# Revit family: V81A-45U-800x1000mm-02.04.14
name_source: partatom
category: Electrical Equipment
revit_build: Autodesk Revit 2013 (Build: 20120221_2030(x64)
units: mm (PartAtom-declared; Revit-internal decimal feet)

## types (1)
- V81A-45U
    Cabinet Depth = 1000 mm  [stored 3.28084 ft]
    Cabinet Height = 2150 mm
    Cabinet Width Overall = 800 mm  [stored 2.62467 ft]
    Color = BLACK
    Description = WARNING: PLEASE RELOAD FAMILY USING THE TYPE CATALOG
    Door Back = Yes
    Door Construction Side = 2
    Door Front = Yes
    Item Class = 1F
    Item Group = RACKS
    Manufacturer = SIEMON
    Metal = SIEMON STEEL
    Model = V81A
    Mounting Rail Material = SIEMON STEEL
    Mounting rail 45 U = SIEMON STEEL
    Ports = 0
    Segment = CSS
    Side Panel Left = Yes
    Side Panel Right = Yes
    System = VPOD
    U Space = 45
    U/M = EA
    Usable Depth = 806 mm  [stored 2.64436 ft]
    Weight = 0.00 lb

note: [stored X ft] marks values corroborated as IEEE doubles in the binary element streams (Revit-internal decimal feet)

## geometry (parser evidence)
native form markers: Blend x16, Sweep x23
no freeform markers — native parametric forms only
